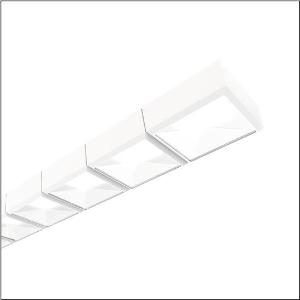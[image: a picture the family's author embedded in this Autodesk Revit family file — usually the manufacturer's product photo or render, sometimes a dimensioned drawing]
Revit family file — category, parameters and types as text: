
# Revit family: scriptus_r__11_5mz212d03wa_20e5
name_source: partatom
category: Lighting Fixtures
units: mm (PartAtom-declared; Revit-internal decimal feet)

## family parameters
Cut with Voids When Loaded = No
Host = Face
Light Source = No
Part Type = Normal
Room Calculation Point = No
Round Connector Dimension = Use Diameter
Shared = No

## types (1)
- Scriptus® 11 (1 x LED 3000K / CRI = 80 (unbekannt), 2200 lm, 3000K)
    Apparent Load = 35 VA
    CIE Flux Codes = 82 95 99 100 100
    Color Rendering = 80
    Color Temperature = 3000K
    Default Elevation = 1800 mm
    Description = Scriptus® 11, office luminaire, primary optical cover: lenses, CAT 2 (L<= 3000cd/m²), light emission: direct distribution, primary light characteristic: symmetric, installation type: surface-mounted, LED, rated luminous flux: 4.390lm, luminous efficacy: 127lm/W, light colour: 830, colour temperature: 3000K, control gear: ECG DALI, with terminal, 5-pole, mains connection: 230V, AC, 50Hz, rated input power: 35W, housing, luminaire housing, of aluminium, traffic white (RAL 9016), length: 1.658mm, width: 114mm, height: 57mm, protection rating (complete): IP20, insulation class (complete): insulation class I (protective earthing), certification: CE, ENEC, VDE, protection symbol: F, permissible operating ambient temperature: 0..+35°C, standard: EN 50419, packaging unit: 1 piece
    Height = 57 mm
    Lamp = 1 x LED 3000K / CRI >= 80 (unbekannt)
    Lamp Light Flux = 2200 lm
    Lamp count = 1
    Length = 1658 mm
    Luminous efficacy = 127 lm/W
    Manufacturer = Siteco
    ModVariant = No
    Model = 5MZ212D03WA
    Mounting Place = Ceiling
    Mounting Type = Surface mounted
    Number of Poles = 1
    OnlyDefault = Yes
    Power Factor = 1
    Product Name = Scriptus® 11
    Product group = office luminaire | ceiling mounted
    ProductGroupID = 304
    Protection Class = Protection class I
    Protection Degree = IP 20
    RLX_Detail_Level = 1
    RLX_Emergency_Light_Flux = 0 lm
    RLX_Emergency_Type = 0
    RLX_Emergency_Type_DB = No
    RlxData = <blob elided: 29489 chars, md5=bfea1e3a>
    Socket = socket
    Standby Power = 0 W
    System Light Flux = 4400 lm
    System Power = 35 W
    Type Comments = Product without accessories
    Type Image = l_1004833.jpg
    URL = http://relux.com
    VarID = ---
    Voltage = 0 V
    Weight = 0.00 kg
    Width = 114 mm

## geometry (parser evidence)
native form markers: Blend x4, Sweep x13
no freeform markers — native parametric forms only
